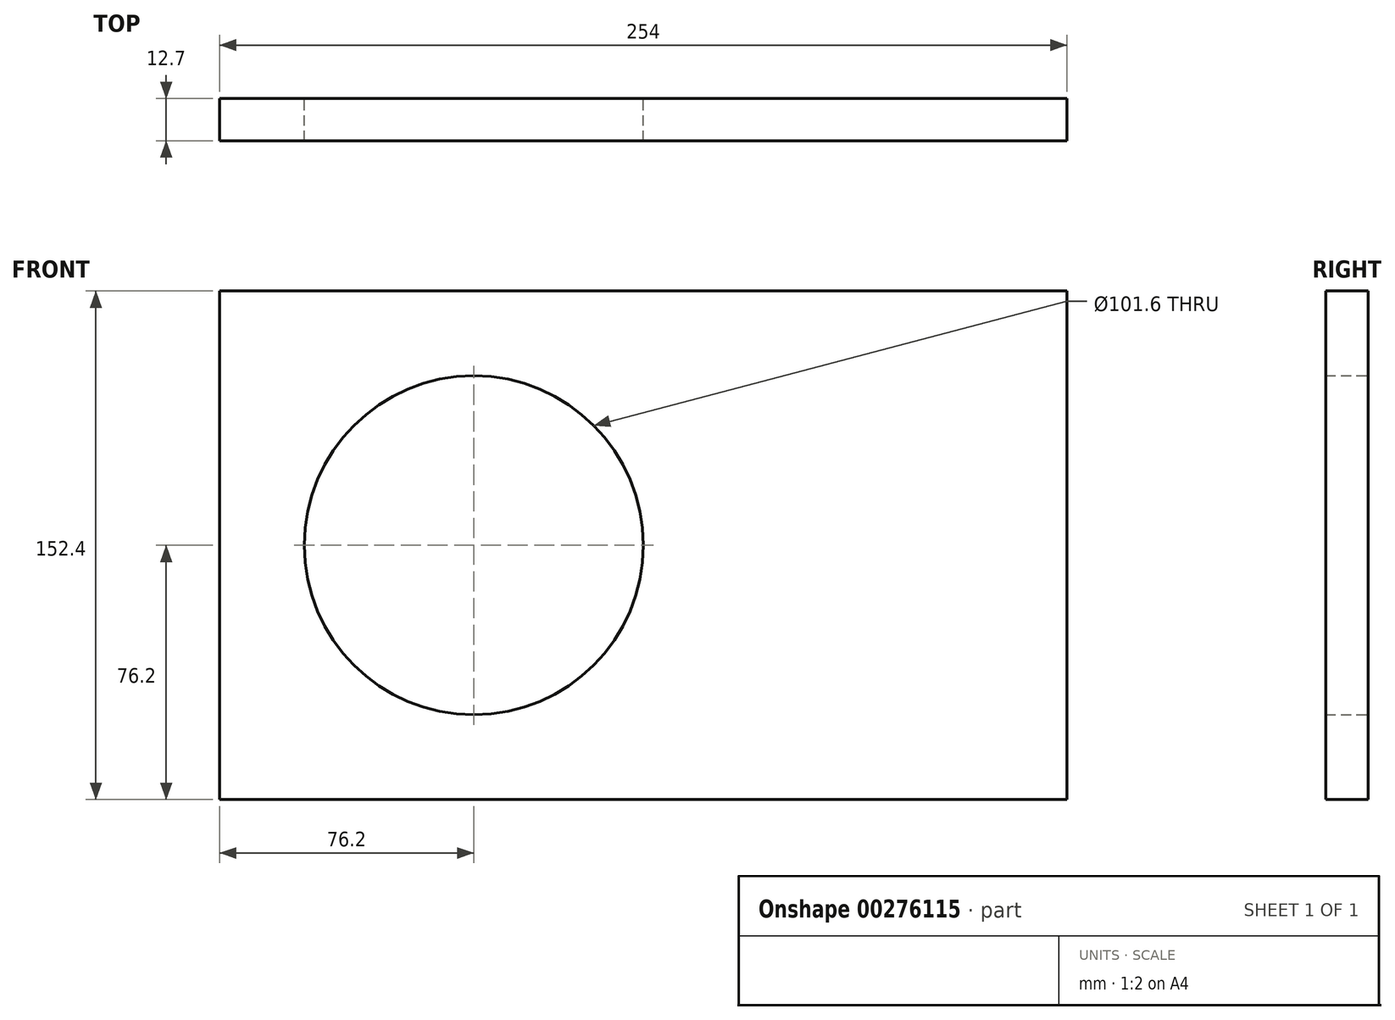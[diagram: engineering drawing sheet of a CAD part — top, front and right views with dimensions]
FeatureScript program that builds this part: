
annotation { "Feature Type Name" : "Feature", "Feature Type Description" : "" }
export const myFeature = defineFeature(function(context is Context, id is Id, definition is map)
    precondition{}
    {
        {
            var Q0;
            Q0=qCreatedBy(makeId("Front.planeOp"),FACE);
            var sketch = newSketch(context, id + "F0", { "sketchPlane" : qUnion([Q0])});
            skLineSegment(sketch, "E0.bottom", {"start": v(-76.2, -76.2) * mm, "end": v(177.8, -76.2) * mm});
            skLineSegment(sketch, "E0.top", {"start": v(-76.2, 76.2) * mm, "end": v(177.8, 76.2) * mm});
            skLineSegment(sketch, "E0.left", {"start": v(-76.2, -76.2) * mm, "end": v(-76.2, 76.2) * mm});
            skLineSegment(sketch, "E0.right", {"start": v(177.8, -76.2) * mm, "end": v(177.8, 76.2) * mm});
            skCircle(sketch, "E1", {"center": v(0, 0) * mm, "radius": 50.8 * mm});
            skSolve(sketch);
        }
        {
            var Q0;
            Q0=makeQuery(id+"F0.imprint","IMPRINT",FACE,{"disambiguationData":[TD([[makeQuery(id+"F0.imprint","IMPRINT",EDGE,{"derivedFrom":sQuery(id+"F0.wireOp",EDGE,"E0.bottom")}),1.0]])]});
            extrude(context, id + "F1", {"entities" : qUnion([Q0]), "depth" : 12.7 * mm});
        }
    });
